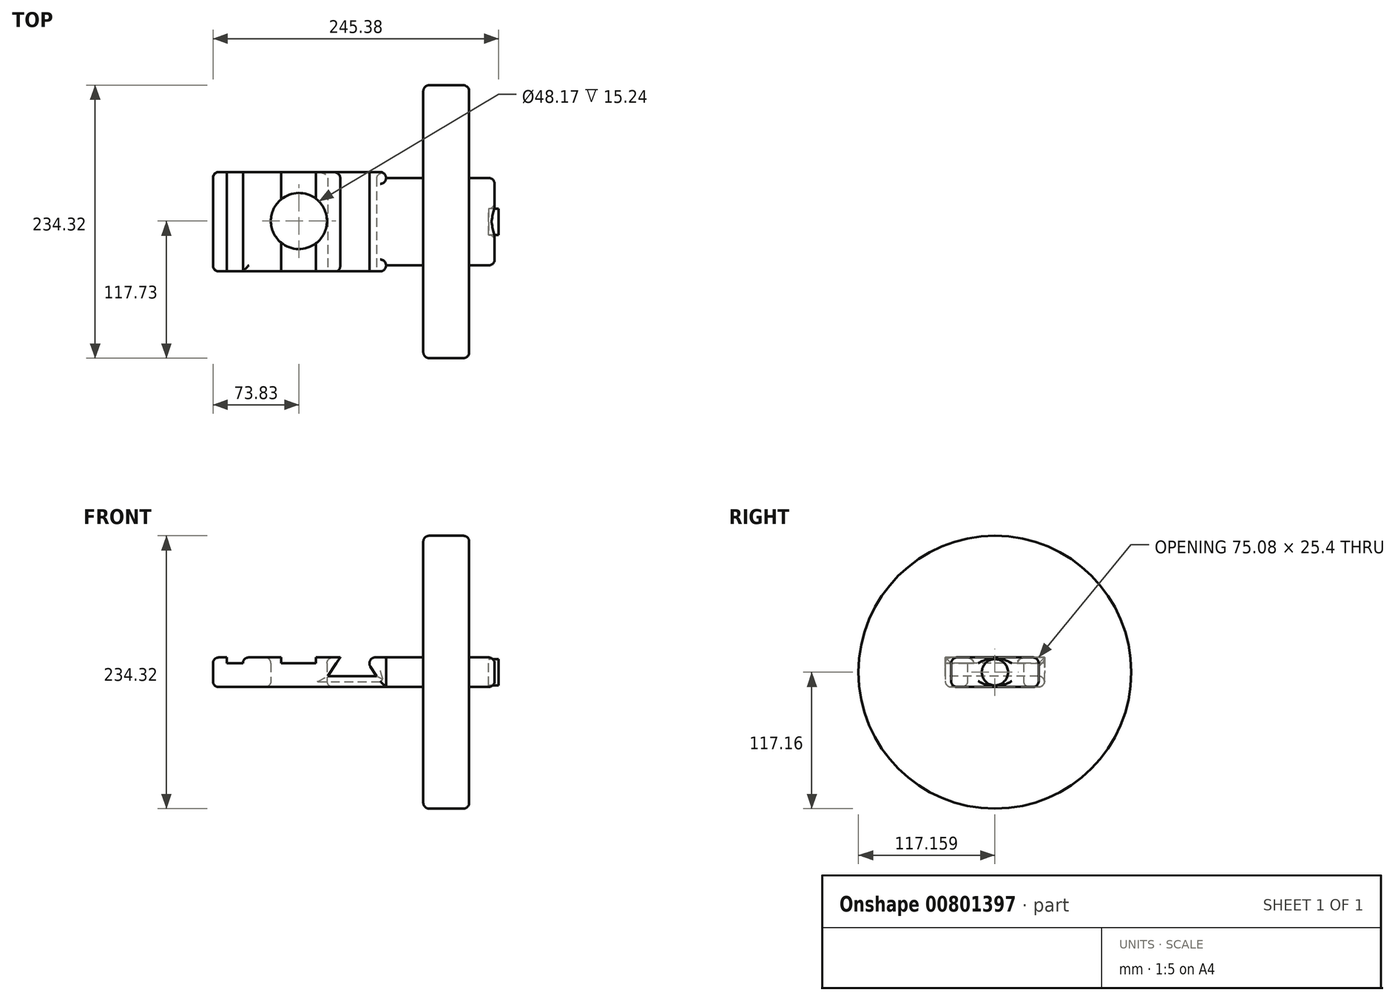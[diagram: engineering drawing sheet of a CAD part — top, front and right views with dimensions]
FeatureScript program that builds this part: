
annotation { "Feature Type Name" : "Feature", "Feature Type Description" : "" }
export const myFeature = defineFeature(function(context is Context, id is Id, definition is map)
    precondition{}
    {
        {
            var Q0;
            Q0=qCreatedBy(makeId("Top.planeOp"),FACE);
            var sketch = newSketch(context, id + "F0", { "sketchPlane" : qUnion([Q0])});
            skLineSegment(sketch, "E0.bottom", {"start": v(-73.83, 42.05) * mm, "end": v(74.78, 42.05) * mm});
            skLineSegment(sketch, "E0.top", {"start": v(-73.83, -43.2) * mm, "end": v(74.78, -43.2) * mm});
            skLineSegment(sketch, "E0.left", {"start": v(-73.83, 42.05) * mm, "end": v(-73.83, -43.2) * mm});
            skLineSegment(sketch, "E0.right", {"start": v(74.78, 42.05) * mm, "end": v(74.78, -43.2) * mm});
            skCircle(sketch, "E1", {"center": v(0, 0) * mm, "radius": 24.08 * mm});
            skSolve(sketch);
        }
        {
            var Q0;
            Q0=makeQuery(id+"F0.imprint","IMPRINT",FACE,{"disambiguationData":[TD([[makeQuery(id+"F0.imprint","IMPRINT",EDGE,{"derivedFrom":sQuery(id+"F0.wireOp",EDGE,"E0.bottom")}),-1.0]])]});
            extrude(context, id + "F1", {"entities" : qUnion([Q0]), "depth" : 25.4 * mm, "offsetDistance" : 25.4 * mm});
        }
        {
            var Q0;
            Q0=makeQuery(id+"F1.opExtrude","CAP_FACE",FACE,{"disambiguationData":[OSD([sQuery(id+"F0.wireOp",EDGE,"E0.bottom"),sQuery(id+"F0.wireOp",EDGE,"E0.top"),sQuery(id+"F0.wireOp",EDGE,"E0.left"),sQuery(id+"F0.wireOp",EDGE,"E0.right"),sQuery(id+"F0.wireOp",EDGE,"E1")])],"isStart":false});
            var sketch = newSketch(context, id + "F2", { "sketchPlane" : qUnion([Q0])});
            skLineSegment(sketch, "E2.bottom", {"start": v(-62.03, 42.05) * mm, "end": v(-48.14, 42.05) * mm});
            skLineSegment(sketch, "E2.top", {"start": v(-62.03, -43.2) * mm, "end": v(-48.14, -43.2) * mm});
            skLineSegment(sketch, "E2.left", {"start": v(-62.03, 42.05) * mm, "end": v(-62.03, -43.2) * mm});
            skLineSegment(sketch, "E2.right", {"start": v(-48.14, 42.05) * mm, "end": v(-48.14, -43.2) * mm});
            skLineSegment(sketch, "E3", {"start": v(14.65, 42.05) * mm, "end": v(14.65, -43.2) * mm});
            skLineSegment(sketch, "E4", {"start": v(-15.44, -43.2) * mm, "end": v(14.65, -43.2) * mm});
            skLineSegment(sketch, "E5", {"start": v(-15.44, -43.2) * mm, "end": v(-15.44, 42.05) * mm});
            skLineSegment(sketch, "E6", {"start": v(14.65, 42.05) * mm, "end": v(-15.44, 42.05) * mm});
            skLineSegment(sketch, "E7", {"start": v(0, 42.05) * mm, "end": v(0, -43.2) * mm, "construction": true});
            skLineSegment(sketch, "E8", {"start": v(0, -43.2) * mm, "end": v(0, 42.05) * mm, "construction": true});
            skSolve(sketch);
        }
        {
            var Q0;
            Q0=makeQuery(id+"F2.imprint","IMPRINT",FACE,{"disambiguationData":[TD([[makeQuery(id+"F2.imprint","IMPRINT",EDGE,{"derivedFrom":sQuery(id+"F2.wireOp",EDGE,"E2.bottom")}),-1.0]])]});
            var Q1;
            {var subQ0=sQuery(id+"F2.wireOp",EDGE,"E4");Q1=makeQuery(id+"F2.imprint","IMPRINT",FACE,{"disambiguationData":[TD([[makeQuery(id+"F2.imprint","IMPRINT",EDGE,{"derivedFrom":subQ0}),1.0]])]});}
            var Q2;
            {var subQ0=sQuery(id+"F2.wireOp",EDGE,"E6");Q2=makeQuery(id+"F2.imprint","IMPRINT",FACE,{"disambiguationData":[TD([[makeQuery(id+"F2.imprint","IMPRINT",EDGE,{"derivedFrom":subQ0}),-1.0]])]});}
            extrude(context, id + "F3", {"entities" : qUnion([Q0, Q1, Q2]), "operationType" : NewBodyOperationType.REMOVE, "oppositeDirection" : true, "depth" : 5.08 * mm, "offsetDistance" : 25.4 * mm});
        }
        {
            var Q0;
            Q0=makeQuery(id+"F1.opExtrude","SWEPT_FACE",FACE,{"disambiguationData":[OSD([sQuery(id+"F0.wireOp",EDGE,"E0.top")])]});
            var sketch = newSketch(context, id + "F4", { "sketchPlane" : qUnion([Q0])});
            skLineSegment(sketch, "E9", {"start": v(35.45, 25.4) * mm, "end": v(24.74, 9.32) * mm});
            skLineSegment(sketch, "E10", {"start": v(24.74, 9.32) * mm, "end": v(66.68, 9.32) * mm});
            skLineSegment(sketch, "E11", {"start": v(66.68, 9.32) * mm, "end": v(56.15, 25.4) * mm});
            skLineSegment(sketch, "E12", {"start": v(56.15, 25.4) * mm, "end": v(35.45, 25.4) * mm});
            skLineSegment(sketch, "E13", {"start": v(45.7, 9.32) * mm, "end": v(45.7, 25.4) * mm, "construction": true});
            skPoint(sketch, "E13.endSnap0", {"position": v(45.7, 9.32) * mm});
            skSolve(sketch);
        }
        {
            var Q0;
            Q0=makeQuery(id+"F4.imprint","IMPRINT",FACE,{"disambiguationData":[TD([[makeQuery(id+"F4.imprint","IMPRINT",EDGE,{"derivedFrom":sQuery(id+"F4.wireOp",EDGE,"E9")}),1.0]])]});
            extrude(context, id + "F5", {"entities" : qUnion([Q0]), "operationType" : NewBodyOperationType.REMOVE, "oppositeDirection" : true, "depth" : 107.44 * mm, "offsetDistance" : 25.4 * mm});
        }
        {
            var Q0;
            Q0=makeQuery(id+"F1.opExtrude","SWEPT_FACE",FACE,{"disambiguationData":[OSD([sQuery(id+"F0.wireOp",EDGE,"E0.right")])]});
            var sketch = newSketch(context, id + "F6", { "sketchPlane" : qUnion([Q0])});
            skCircle(sketch, "E14", {"center": v(-0.57, 12.7) * mm, "radius": 11.27 * mm});
            skPoint(sketch, "E14.centerSnap0", {"position": v(-43.2, 12.7) * mm});
            skPoint(sketch, "E14.centerSnap1", {"position": v(-0.57, 25.4) * mm});
            skSolve(sketch);
        }
        {
            var Q0;
            Q0=makeQuery(id+"F6.imprint","IMPRINT",FACE,{"disambiguationData":[TD([[makeQuery(id+"F6.imprint","IMPRINT",EDGE,{"derivedFrom":sQuery(id+"F6.wireOp",EDGE,"E14")}),1.0]])]});
            extrude(context, id + "F7", {"entities" : qUnion([Q0]), "operationType" : NewBodyOperationType.ADD, "depth" : 71.37 * mm, "offsetDistance" : 25.4 * mm});
        }
        {
            var Q0;
            Q0=makeQuery(id+"F7.opExtrude","CAP_EDGE",EDGE,{"disambiguationData":[OSD([sQuery(id+"F6.wireOp",EDGE,"E14")])],"isStart":false});
            var Q1;
            Q1=makeQuery(id+"F7.opExtrude","CAP_EDGE",EDGE,{"disambiguationData":[OSD([sQuery(id+"F6.wireOp",EDGE,"E14")])],"isStart":true});
            var Q2;
            Q2=makeQuery(id+"F1.opExtrude","SWEPT_EDGE",EDGE,{"disambiguationData":[OSD([sQuery(id+"F0.wireOp",EDGE,"E0.top"),sQuery(id+"F0.wireOp",EDGE,"E0.right")])]});
            var Q3;
            Q3=makeQuery(id+"F1.opExtrude","SWEPT_EDGE",EDGE,{"disambiguationData":[OSD([sQuery(id+"F0.wireOp",EDGE,"E0.bottom"),sQuery(id+"F0.wireOp",EDGE,"E0.right")])]});
            var Q4;
            Q4=makeQuery(id+"F5.boolean.opBoolean","COPY",EDGE,{"derivedFrom":makeQuery(id+"F5.opExtrude","SWEPT_EDGE",EDGE,{"disambiguationData":[OSD([sQuery(id+"F0.wireOp",EDGE,"E0.top"),sQuery(id+"F4.wireOp",EDGE,"E11"),sQuery(id+"F4.wireOp",EDGE,"E12")])]})});
            var Q5;
            Q5=makeQuery(id+"F5.boolean.opBoolean","COPY",EDGE,{"derivedFrom":makeQuery(id+"F5.opExtrude","SWEPT_EDGE",EDGE,{"disambiguationData":[OSD([sQuery(id+"F0.wireOp",EDGE,"E0.top"),sQuery(id+"F4.wireOp",EDGE,"E9"),sQuery(id+"F4.wireOp",EDGE,"E12")])]})});
            var Q6;
            Q6=makeQuery(id+"F5.boolean.opBoolean","INTERSECT",EDGE,{"derivedFrom":[makeQuery(id+"F1.opExtrude","SWEPT_FACE",FACE,{"disambiguationData":[OSD([sQuery(id+"F0.wireOp",EDGE,"E0.bottom")])]}),makeQuery(id+"F5.opExtrude","SWEPT_FACE",FACE,{"disambiguationData":[OSD([sQuery(id+"F4.wireOp",EDGE,"E10")])]})]});
            var Q7;
            Q7=makeQuery(id+"F5.boolean.opBoolean","COPY",EDGE,{"derivedFrom":makeQuery(id+"F5.opExtrude","CAP_EDGE",EDGE,{"disambiguationData":[OSD([sQuery(id+"F4.wireOp",EDGE,"E9")])],"isStart":true})});
            var Q8;
            Q8=makeQuery(id+"F5.boolean.opBoolean","COPY",EDGE,{"derivedFrom":makeQuery(id+"F5.opExtrude","CAP_EDGE",EDGE,{"disambiguationData":[OSD([sQuery(id+"F4.wireOp",EDGE,"E10")])],"isStart":true})});
            var Q9;
            Q9=makeQuery(id+"F5.boolean.opBoolean","COPY",EDGE,{"derivedFrom":makeQuery(id+"F5.opExtrude","CAP_EDGE",EDGE,{"disambiguationData":[OSD([sQuery(id+"F4.wireOp",EDGE,"E11")])],"isStart":true})});
            var Q10;
            Q10=makeQuery(id+"F5.boolean.opBoolean","INTERSECT",EDGE,{"derivedFrom":[makeQuery(id+"F1.opExtrude","SWEPT_FACE",FACE,{"disambiguationData":[OSD([sQuery(id+"F0.wireOp",EDGE,"E0.bottom")])]}),makeQuery(id+"F5.opExtrude","SWEPT_FACE",FACE,{"disambiguationData":[OSD([sQuery(id+"F4.wireOp",EDGE,"E11")])]})]});
            var Q11;
            Q11=makeQuery(id+"F5.boolean.opBoolean","INTERSECT",EDGE,{"derivedFrom":[makeQuery(id+"F1.opExtrude","SWEPT_FACE",FACE,{"disambiguationData":[OSD([sQuery(id+"F0.wireOp",EDGE,"E0.bottom")])]}),makeQuery(id+"F5.opExtrude","SWEPT_FACE",FACE,{"disambiguationData":[OSD([sQuery(id+"F4.wireOp",EDGE,"E9")])]})]});
            var Q12;
            {var subQ1=sQuery(id+"F0.wireOp",EDGE,"E0.right");var subQ2=sQuery(id+"F0.wireOp",EDGE,"E0.top");var subQ6=makeQuery(id+"F1.opExtrude","CAP_EDGE",EDGE,{"disambiguationData":[OSD([subQ2])],"isStart":false});Q12=makeQuery(id+"F5.boolean.opBoolean","SPLIT",EDGE,{"disambiguationData":[TD([makeQuery(id+"F5.opExtrude","SWEPT_FACE",FACE,{"disambiguationData":[OSD([sQuery(id+"F4.wireOp",EDGE,"E9")])]})])],"derivedFrom":makeQuery(id+"F3.boolean.opBoolean","SPLIT",EDGE,{"disambiguationData":[TD([makeQuery(id+"F1.opExtrude","SWEPT_FACE",FACE,{"disambiguationData":[OSD([subQ1])]})])],"derivedFrom":subQ6})});}
            var Q13;
            Q13=makeQuery(id+"F3.boolean.opBoolean","COPY",EDGE,{"derivedFrom":makeQuery(id+"F3.opExtrude","CAP_EDGE",EDGE,{"disambiguationData":[OSD([sQuery(id+"F2.wireOp",EDGE,"E4")])],"isStart":false})});
            var Q14;
            {var subQ0=sQuery(id+"F0.wireOp",EDGE,"E1");var subQ3=sQuery(id+"F2.wireOp",EDGE,"E3");var subQ4=makeQuery(id+"F1.opExtrude","CAP_EDGE",EDGE,{"disambiguationData":[OSD([subQ0])],"isStart":false});Q14=makeQuery(id+"F3.boolean.opBoolean","SPLIT",EDGE,{"disambiguationData":[TD([makeQuery(id+"F3.opExtrude","SWEPT_FACE",FACE,{"disambiguationData":[OSD([subQ3]),TDD([makeQuery(id+"F2.imprint","IMPRINT",EDGE,{"disambiguationData":[TD([[makeQuery(id+"F2.imprint","INTERSECT",VERTEX,{"disambiguationData":[OD(0.0)],"derivedFrom":[subQ4,subQ3]}),1.0]])],"derivedFrom":subQ3})])]})])],"derivedFrom":subQ4});}
            var Q15;
            Q15=makeQuery(id+"F3.boolean.opBoolean","COPY",EDGE,{"derivedFrom":makeQuery(id+"F3.opExtrude","SWEPT_EDGE",EDGE,{"disambiguationData":[OSD([sQuery(id+"F0.wireOp",EDGE,"E0.bottom"),sQuery(id+"F2.wireOp",EDGE,"E3"),sQuery(id+"F2.wireOp",EDGE,"E6")])]})});
            var Q16;
            Q16=makeQuery(id+"F3.boolean.opBoolean","COPY",EDGE,{"derivedFrom":makeQuery(id+"F3.opExtrude","CAP_EDGE",EDGE,{"disambiguationData":[OSD([sQuery(id+"F2.wireOp",EDGE,"E6")])],"isStart":false})});
            var Q17;
            Q17=makeQuery(id+"F3.boolean.opBoolean","COPY",EDGE,{"derivedFrom":makeQuery(id+"F3.opExtrude","SWEPT_EDGE",EDGE,{"disambiguationData":[OSD([sQuery(id+"F0.wireOp",EDGE,"E0.top"),sQuery(id+"F2.wireOp",EDGE,"E3"),sQuery(id+"F2.wireOp",EDGE,"E4")])]})});
            var Q18;
            Q18=makeQuery(id+"F1.opExtrude","CAP_EDGE",EDGE,{"disambiguationData":[OSD([sQuery(id+"F0.wireOp",EDGE,"E1")])],"isStart":true});
            var Q19;
            {var subQ0=sQuery(id+"F0.wireOp",EDGE,"E1");var subQ3=sQuery(id+"F2.wireOp",EDGE,"E5");var subQ4=makeQuery(id+"F1.opExtrude","CAP_EDGE",EDGE,{"disambiguationData":[OSD([subQ0])],"isStart":false});Q19=makeQuery(id+"F3.boolean.opBoolean","SPLIT",EDGE,{"disambiguationData":[TD([makeQuery(id+"F3.opExtrude","SWEPT_FACE",FACE,{"disambiguationData":[OSD([subQ3]),TDD([makeQuery(id+"F2.imprint","IMPRINT",EDGE,{"disambiguationData":[TD([[makeQuery(id+"F2.imprint","INTERSECT",VERTEX,{"disambiguationData":[OD(0.0)],"derivedFrom":[subQ4,subQ3]}),1.0]])],"derivedFrom":subQ3})])]})])],"derivedFrom":subQ4});}
            var Q20;
            {var subQ0=sQuery(id+"F2.wireOp",EDGE,"E5");var subQ1=sQuery(id+"F0.wireOp",EDGE,"E1");Q20=makeQuery(id+"F3.boolean.opBoolean","COPY",EDGE,{"derivedFrom":makeQuery(id+"F3.opExtrude","SWEPT_EDGE",EDGE,{"disambiguationData":[OSD([subQ1,subQ0]),TDD([makeQuery(id+"F2.imprint","INTERSECT",VERTEX,{"disambiguationData":[OD(1.0)],"derivedFrom":[makeQuery(id+"F1.opExtrude","CAP_EDGE",EDGE,{"disambiguationData":[OSD([subQ1])],"isStart":false}),subQ0]})])]})});}
            var Q21;
            {var subQ0=sQuery(id+"F2.wireOp",EDGE,"E5");var subQ1=sQuery(id+"F0.wireOp",EDGE,"E1");Q21=makeQuery(id+"F3.boolean.opBoolean","COPY",EDGE,{"derivedFrom":makeQuery(id+"F3.opExtrude","SWEPT_EDGE",EDGE,{"disambiguationData":[OSD([subQ1,subQ0]),TDD([makeQuery(id+"F2.imprint","INTERSECT",VERTEX,{"disambiguationData":[OD(0.0)],"derivedFrom":[makeQuery(id+"F1.opExtrude","CAP_EDGE",EDGE,{"disambiguationData":[OSD([subQ1])],"isStart":false}),subQ0]})])]})});}
            var Q22;
            Q22=makeQuery(id+"F3.boolean.opBoolean","COPY",EDGE,{"derivedFrom":makeQuery(id+"F3.opExtrude","SWEPT_EDGE",EDGE,{"disambiguationData":[OSD([sQuery(id+"F0.wireOp",EDGE,"E0.top"),sQuery(id+"F2.wireOp",EDGE,"E4"),sQuery(id+"F2.wireOp",EDGE,"E5")])]})});
            var Q23;
            Q23=makeQuery(id+"F3.boolean.opBoolean","COPY",EDGE,{"derivedFrom":makeQuery(id+"F3.opExtrude","SWEPT_EDGE",EDGE,{"disambiguationData":[OSD([sQuery(id+"F0.wireOp",EDGE,"E0.bottom"),sQuery(id+"F2.wireOp",EDGE,"E5"),sQuery(id+"F2.wireOp",EDGE,"E6")])]})});
            var Q24;
            {var subQ1=sQuery(id+"F0.wireOp",EDGE,"E0.top");var subQ3=makeQuery(id+"F1.opExtrude","CAP_EDGE",EDGE,{"disambiguationData":[OSD([subQ1])],"isStart":false});Q24=makeQuery(id+"F3.boolean.opBoolean","SPLIT",EDGE,{"disambiguationData":[TD([makeQuery(id+"F3.opExtrude","SWEPT_FACE",FACE,{"disambiguationData":[OSD([sQuery(id+"F2.wireOp",EDGE,"E2.right")])]})])],"derivedFrom":subQ3});}
            var Q25;
            Q25=makeQuery(id+"F3.boolean.opBoolean","COPY",EDGE,{"derivedFrom":makeQuery(id+"F3.opExtrude","CAP_EDGE",EDGE,{"disambiguationData":[OSD([sQuery(id+"F2.wireOp",EDGE,"E2.right")])],"isStart":true})});
            var Q26;
            Q26=makeQuery(id+"F3.boolean.opBoolean","COPY",EDGE,{"derivedFrom":makeQuery(id+"F3.opExtrude","SWEPT_EDGE",EDGE,{"disambiguationData":[OSD([sQuery(id+"F0.wireOp",EDGE,"E0.bottom"),sQuery(id+"F2.wireOp",EDGE,"E2.bottom"),sQuery(id+"F2.wireOp",EDGE,"E2.right")])]})});
            var Q27;
            Q27=makeQuery(id+"F3.boolean.opBoolean","COPY",EDGE,{"derivedFrom":makeQuery(id+"F3.opExtrude","CAP_EDGE",EDGE,{"disambiguationData":[OSD([sQuery(id+"F2.wireOp",EDGE,"E2.bottom")])],"isStart":false})});
            var Q28;
            Q28=makeQuery(id+"F3.boolean.opBoolean","COPY",EDGE,{"derivedFrom":makeQuery(id+"F3.opExtrude","SWEPT_EDGE",EDGE,{"disambiguationData":[OSD([sQuery(id+"F0.wireOp",EDGE,"E0.top"),sQuery(id+"F2.wireOp",EDGE,"E2.top"),sQuery(id+"F2.wireOp",EDGE,"E2.right")])]})});
            var Q29;
            Q29=makeQuery(id+"F3.boolean.opBoolean","COPY",EDGE,{"derivedFrom":makeQuery(id+"F3.opExtrude","CAP_EDGE",EDGE,{"disambiguationData":[OSD([sQuery(id+"F2.wireOp",EDGE,"E2.top")])],"isStart":false})});
            var Q30;
            Q30=makeQuery(id+"F3.boolean.opBoolean","COPY",EDGE,{"derivedFrom":makeQuery(id+"F3.opExtrude","SWEPT_EDGE",EDGE,{"disambiguationData":[OSD([sQuery(id+"F0.wireOp",EDGE,"E0.bottom"),sQuery(id+"F2.wireOp",EDGE,"E2.bottom"),sQuery(id+"F2.wireOp",EDGE,"E2.left")])]})});
            var Q31;
            Q31=makeQuery(id+"F1.opExtrude","SWEPT_EDGE",EDGE,{"disambiguationData":[OSD([sQuery(id+"F0.wireOp",EDGE,"E0.top"),sQuery(id+"F0.wireOp",EDGE,"E0.left")])]});
            var Q32;
            Q32=makeQuery(id+"F1.opExtrude","CAP_EDGE",EDGE,{"disambiguationData":[OSD([sQuery(id+"F0.wireOp",EDGE,"E0.left")])],"isStart":true});
            var Q33;
            Q33=makeQuery(id+"F1.opExtrude","SWEPT_EDGE",EDGE,{"disambiguationData":[OSD([sQuery(id+"F0.wireOp",EDGE,"E0.bottom"),sQuery(id+"F0.wireOp",EDGE,"E0.left")])]});
            var Q34;
            Q34=makeQuery(id+"F1.opExtrude","CAP_EDGE",EDGE,{"disambiguationData":[OSD([sQuery(id+"F0.wireOp",EDGE,"E0.top")])],"isStart":true});
            var Q35;
            Q35=makeQuery(id+"F1.opExtrude","CAP_EDGE",EDGE,{"disambiguationData":[OSD([sQuery(id+"F0.wireOp",EDGE,"E0.bottom")])],"isStart":true});
            var Q36;
            Q36=makeQuery(id+"F1.opExtrude","CAP_EDGE",EDGE,{"disambiguationData":[OSD([sQuery(id+"F0.wireOp",EDGE,"E0.left")])],"isStart":false});
            var Q37;
            {var subQ0=sQuery(id+"F2.wireOp",EDGE,"E3");var subQ1=sQuery(id+"F0.wireOp",EDGE,"E1");Q37=makeQuery(id+"F3.boolean.opBoolean","COPY",EDGE,{"derivedFrom":makeQuery(id+"F3.opExtrude","SWEPT_EDGE",EDGE,{"disambiguationData":[OSD([subQ1,subQ0]),TDD([makeQuery(id+"F2.imprint","INTERSECT",VERTEX,{"disambiguationData":[OD(1.0)],"derivedFrom":[makeQuery(id+"F1.opExtrude","CAP_EDGE",EDGE,{"disambiguationData":[OSD([subQ1])],"isStart":false}),subQ0]})])]})});}
            fillet(context, id + "F8", {"entities" : qUnion([Q0, Q1, Q2, Q3, Q4, Q5, Q6, Q7, Q8, Q9, Q10, Q11, Q12, Q13, Q14, Q15, Q16, Q17, Q18, Q19, Q20, Q21, Q22, Q23, Q24, Q25, Q26, Q27, Q28, Q29, Q30, Q31, Q32, Q33, Q34, Q35, Q36, Q37]), "radius" : 5.08 * mm, "tangentPropagation" : true, "allowEdgeOverflow" : false});
        }
        {
            var Q0;
            Q0=makeQuery(id+"F8.opFillet","SPLIT",FACE,{"disambiguationData":[OD(1.0)],"derivedFrom":makeQuery(id+"F1.opExtrude","SWEPT_FACE",FACE,{"disambiguationData":[OSD([sQuery(id+"F0.wireOp",EDGE,"E0.right")])]})});
            var Q1;
            Q1=makeQuery(id+"F8.opFillet","SPLIT",FACE,{"disambiguationData":[OD(0.0)],"derivedFrom":makeQuery(id+"F1.opExtrude","SWEPT_FACE",FACE,{"disambiguationData":[OSD([sQuery(id+"F0.wireOp",EDGE,"E0.right")])]})});
            extrude(context, id + "F9", {"entities" : qUnion([Q0, Q1]), "operationType" : NewBodyOperationType.ADD, "depth" : 93.22 * mm, "offsetDistance" : 25.4 * mm});
        }
        {
            var Q0;
            {var subQ0=sQuery(id+"F0.wireOp",EDGE,"E0.right");var subQ1=makeQuery(id+"F1.opExtrude","SWEPT_FACE",FACE,{"disambiguationData":[OSD([subQ0])]});var subQ2=sQuery(id+"F0.wireOp",EDGE,"E0.bottom");var subQ4=sQuery(id+"F0.wireOp",EDGE,"E0.top");var subQ6=sQuery(id+"F0.wireOp",EDGE,"E1");var subQ9=sQuery(id+"F0.wireOp",EDGE,"E0.left");Q0=makeQuery(id+"F9.opExtrude","SWEPT_EDGE",EDGE,{"disambiguationData":[OSD([subQ2,subQ4,subQ9,subQ0,subQ6]),TDD([makeQuery(id+"F8.opFillet","BLEND_VERTEX",VERTEX,{"blendedFrom":[makeQuery(id+"F1.opExtrude","SWEPT_EDGE",EDGE,{"disambiguationData":[OSD([subQ4,subQ0])]}),makeQuery(id+"F5.boolean.opBoolean","SPLIT",FACE,{"disambiguationData":[TD([subQ1])],"derivedFrom":makeQuery(id+"F3.boolean.opBoolean","SPLIT",FACE,{"disambiguationData":[TD([subQ1])],"derivedFrom":makeQuery(id+"F1.opExtrude","CAP_FACE",FACE,{"disambiguationData":[OSD([subQ2,subQ4,subQ9,subQ0,subQ6])],"isStart":false})})}),subQ1],"blendedInto":[makeQuery(id+"F5.boolean.opBoolean","SPLIT",FACE,{"disambiguationData":[TD([subQ1])],"derivedFrom":makeQuery(id+"F3.boolean.opBoolean","SPLIT",FACE,{"disambiguationData":[TD([subQ1])],"derivedFrom":makeQuery(id+"F1.opExtrude","CAP_FACE",FACE,{"disambiguationData":[OSD([subQ2,subQ4,subQ9,subQ0,subQ6])],"isStart":false})})}),subQ1]})])]});}
            var Q1;
            {var subQ0=sQuery(id+"F0.wireOp",EDGE,"E0.right");var subQ1=sQuery(id+"F0.wireOp",EDGE,"E1");var subQ2=sQuery(id+"F0.wireOp",EDGE,"E0.left");var subQ3=sQuery(id+"F0.wireOp",EDGE,"E0.top");var subQ4=sQuery(id+"F0.wireOp",EDGE,"E0.bottom");Q1=makeQuery(id+"F9.opExtrude","SWEPT_EDGE",EDGE,{"disambiguationData":[OSD([subQ4,subQ3,subQ2,subQ0,subQ1]),TDD([makeQuery(id+"F8.opFillet","BLEND_VERTEX",VERTEX,{"blendedFrom":[makeQuery(id+"F1.opExtrude","SWEPT_EDGE",EDGE,{"disambiguationData":[OSD([subQ3,subQ0])]}),makeQuery(id+"F1.opExtrude","CAP_EDGE",EDGE,{"disambiguationData":[OSD([subQ3])],"isStart":true}),makeQuery(id+"F1.opExtrude","CAP_FACE",FACE,{"disambiguationData":[OSD([subQ4,subQ3,subQ2,subQ0,subQ1])],"isStart":true}),makeQuery(id+"F1.opExtrude","SWEPT_FACE",FACE,{"disambiguationData":[OSD([subQ0])]})],"blendedInto":[makeQuery(id+"F1.opExtrude","CAP_FACE",FACE,{"disambiguationData":[OSD([subQ4,subQ3,subQ2,subQ0,subQ1])],"isStart":true}),makeQuery(id+"F1.opExtrude","SWEPT_FACE",FACE,{"disambiguationData":[OSD([subQ0])]})]})])]});}
            var Q2;
            Q2=makeQuery(id+"F9.opExtrude","CAP_EDGE",EDGE,{"disambiguationData":[OSD([sQuery(id+"F0.wireOp",EDGE,"E0.top"),sQuery(id+"F0.wireOp",EDGE,"E0.right")])],"isStart":false});
            var Q3;
            {var subQ0=sQuery(id+"F0.wireOp",EDGE,"E0.right");Q3=makeQuery(id+"F9.opExtrude","CAP_EDGE",EDGE,{"disambiguationData":[OSD([subQ0]),TDD([makeQuery(id+"F1.opExtrude","CAP_EDGE",EDGE,{"disambiguationData":[OSD([subQ0])],"isStart":true})])],"isStart":false});}
            var Q4;
            {var subQ0=sQuery(id+"F0.wireOp",EDGE,"E0.right");Q4=makeQuery(id+"F9.opExtrude","CAP_EDGE",EDGE,{"disambiguationData":[OSD([subQ0]),TDD([makeQuery(id+"F1.opExtrude","CAP_EDGE",EDGE,{"disambiguationData":[OSD([subQ0])],"isStart":false})])],"isStart":false});}
            var Q5;
            {var subQ0=sQuery(id+"F0.wireOp",EDGE,"E0.right");var subQ1=sQuery(id+"F6.wireOp",EDGE,"E14");Q5=makeQuery(id+"F9.opExtrude","CAP_EDGE",EDGE,{"disambiguationData":[OSD([subQ0,subQ1]),TDD([makeQuery(id+"F8.opFillet","BLEND_EDGE",EDGE,{"disambiguationData":[OD(1.0)],"blendedFrom":[makeQuery(id+"F7.opExtrude","CAP_EDGE",EDGE,{"disambiguationData":[OSD([subQ1])],"isStart":true}),makeQuery(id+"F1.opExtrude","SWEPT_FACE",FACE,{"disambiguationData":[OSD([subQ0])]})],"blendedInto":[makeQuery(id+"F1.opExtrude","SWEPT_FACE",FACE,{"disambiguationData":[OSD([subQ0])]})]})])],"isStart":false});}
            var Q6;
            {var subQ0=sQuery(id+"F0.wireOp",EDGE,"E0.right");var subQ1=sQuery(id+"F6.wireOp",EDGE,"E14");Q6=makeQuery(id+"F9.opExtrude","CAP_EDGE",EDGE,{"disambiguationData":[OSD([subQ0,subQ1]),TDD([makeQuery(id+"F8.opFillet","BLEND_EDGE",EDGE,{"disambiguationData":[OD(0.0)],"blendedFrom":[makeQuery(id+"F7.opExtrude","CAP_EDGE",EDGE,{"disambiguationData":[OSD([subQ1])],"isStart":true}),makeQuery(id+"F1.opExtrude","SWEPT_FACE",FACE,{"disambiguationData":[OSD([subQ0])]})],"blendedInto":[makeQuery(id+"F1.opExtrude","SWEPT_FACE",FACE,{"disambiguationData":[OSD([subQ0])]})]})])],"isStart":false});}
            var Q7;
            {var subQ0=sQuery(id+"F0.wireOp",EDGE,"E0.right");var subQ1=makeQuery(id+"F1.opExtrude","SWEPT_FACE",FACE,{"disambiguationData":[OSD([subQ0])]});var subQ2=sQuery(id+"F0.wireOp",EDGE,"E0.bottom");var subQ4=sQuery(id+"F0.wireOp",EDGE,"E0.top");var subQ6=sQuery(id+"F0.wireOp",EDGE,"E1");var subQ9=sQuery(id+"F0.wireOp",EDGE,"E0.left");Q7=makeQuery(id+"F9.opExtrude","SWEPT_EDGE",EDGE,{"disambiguationData":[OSD([subQ2,subQ4,subQ9,subQ0,subQ6]),TDD([makeQuery(id+"F8.opFillet","BLEND_VERTEX",VERTEX,{"blendedFrom":[makeQuery(id+"F1.opExtrude","SWEPT_EDGE",EDGE,{"disambiguationData":[OSD([subQ2,subQ0])]}),makeQuery(id+"F5.boolean.opBoolean","SPLIT",FACE,{"disambiguationData":[TD([subQ1])],"derivedFrom":makeQuery(id+"F3.boolean.opBoolean","SPLIT",FACE,{"disambiguationData":[TD([subQ1])],"derivedFrom":makeQuery(id+"F1.opExtrude","CAP_FACE",FACE,{"disambiguationData":[OSD([subQ2,subQ4,subQ9,subQ0,subQ6])],"isStart":false})})}),subQ1],"blendedInto":[makeQuery(id+"F5.boolean.opBoolean","SPLIT",FACE,{"disambiguationData":[TD([subQ1])],"derivedFrom":makeQuery(id+"F3.boolean.opBoolean","SPLIT",FACE,{"disambiguationData":[TD([subQ1])],"derivedFrom":makeQuery(id+"F1.opExtrude","CAP_FACE",FACE,{"disambiguationData":[OSD([subQ2,subQ4,subQ9,subQ0,subQ6])],"isStart":false})})}),subQ1]})])]});}
            var Q8;
            {var subQ0=sQuery(id+"F0.wireOp",EDGE,"E0.right");var subQ1=sQuery(id+"F0.wireOp",EDGE,"E1");var subQ2=sQuery(id+"F0.wireOp",EDGE,"E0.left");var subQ3=sQuery(id+"F0.wireOp",EDGE,"E0.top");var subQ4=sQuery(id+"F0.wireOp",EDGE,"E0.bottom");Q8=makeQuery(id+"F9.opExtrude","SWEPT_EDGE",EDGE,{"disambiguationData":[OSD([subQ4,subQ3,subQ2,subQ0,subQ1]),TDD([makeQuery(id+"F8.opFillet","BLEND_VERTEX",VERTEX,{"blendedFrom":[makeQuery(id+"F1.opExtrude","SWEPT_EDGE",EDGE,{"disambiguationData":[OSD([subQ4,subQ0])]}),makeQuery(id+"F1.opExtrude","CAP_EDGE",EDGE,{"disambiguationData":[OSD([subQ4])],"isStart":true}),makeQuery(id+"F1.opExtrude","CAP_FACE",FACE,{"disambiguationData":[OSD([subQ4,subQ3,subQ2,subQ0,subQ1])],"isStart":true}),makeQuery(id+"F1.opExtrude","SWEPT_FACE",FACE,{"disambiguationData":[OSD([subQ0])]})],"blendedInto":[makeQuery(id+"F1.opExtrude","CAP_FACE",FACE,{"disambiguationData":[OSD([subQ4,subQ3,subQ2,subQ0,subQ1])],"isStart":true}),makeQuery(id+"F1.opExtrude","SWEPT_FACE",FACE,{"disambiguationData":[OSD([subQ0])]})]})])]});}
            var Q9;
            Q9=makeQuery(id+"F9.opExtrude","CAP_EDGE",EDGE,{"disambiguationData":[OSD([sQuery(id+"F0.wireOp",EDGE,"E0.bottom"),sQuery(id+"F0.wireOp",EDGE,"E0.right")])],"isStart":false});
            fillet(context, id + "F10", {"entities" : qUnion([Q0, Q1, Q2, Q3, Q4, Q5, Q6, Q7, Q8, Q9]), "radius" : 5.08 * mm, "tangentPropagation" : true, "allowEdgeOverflow" : false});
        }
        {
            var Q0;
            Q0=makeQuery(id+"F7.opExtrude","CAP_FACE",FACE,{"disambiguationData":[OSD([sQuery(id+"F6.wireOp",EDGE,"E14")])],"isStart":false});
            var sketch = newSketch(context, id + "F11", { "sketchPlane" : qUnion([Q0])});
            skCircle(sketch, "E15", {"center": v(-0.57, 12.7) * mm, "radius": 117.16 * mm});
            skSolve(sketch);
        }
        {
            var Q0;
            Q0=makeQuery(id+"F11.imprint","IMPRINT",FACE,{"disambiguationData":[TD([[makeQuery(id+"F11.imprint","IMPRINT",EDGE,{"derivedFrom":sQuery(id+"F11.wireOp",EDGE,"E15")}),1.0]])]});
            extrude(context, id + "F12", {"entities" : qUnion([Q0]), "operationType" : NewBodyOperationType.ADD, "oppositeDirection" : true, "depth" : 39.37 * mm, "offsetDistance" : 25.4 * mm});
        }
        {
            var Q0;
            Q0=makeQuery(id+"F12.opExtrude","CAP_EDGE",EDGE,{"disambiguationData":[OSD([sQuery(id+"F11.wireOp",EDGE,"E15")])],"isStart":true});
            var Q1;
            Q1=makeQuery(id+"F12.opExtrude","CAP_EDGE",EDGE,{"disambiguationData":[OSD([sQuery(id+"F11.wireOp",EDGE,"E15")])],"isStart":false});
            fillet(context, id + "F13", {"entities" : qUnion([Q0, Q1]), "radius" : 5.08 * mm, "tangentPropagation" : true, "allowEdgeOverflow" : false});
        }
        {
            var Q0;
            {var subQ0=sQuery(id+"F6.wireOp",EDGE,"E14");Q0=makeQuery(id+"F12.boolean.opBoolean","MERGE",FACE,{"derivedFrom":[makeQuery(id+"F7.opExtrude","CAP_FACE",FACE,{"disambiguationData":[OSD([subQ0])],"isStart":false}),makeQuery(id+"F12.opExtrude","CAP_FACE",FACE,{"disambiguationData":[OSD([subQ0,sQuery(id+"F11.wireOp",EDGE,"E15")])],"isStart":true})]});}
            extrude(context, id + "F14", {"entities" : qUnion([Q0]), "operationType" : NewBodyOperationType.ADD, "depth" : 25.4 * mm, "offsetDistance" : 25.4 * mm});
        }
    });
